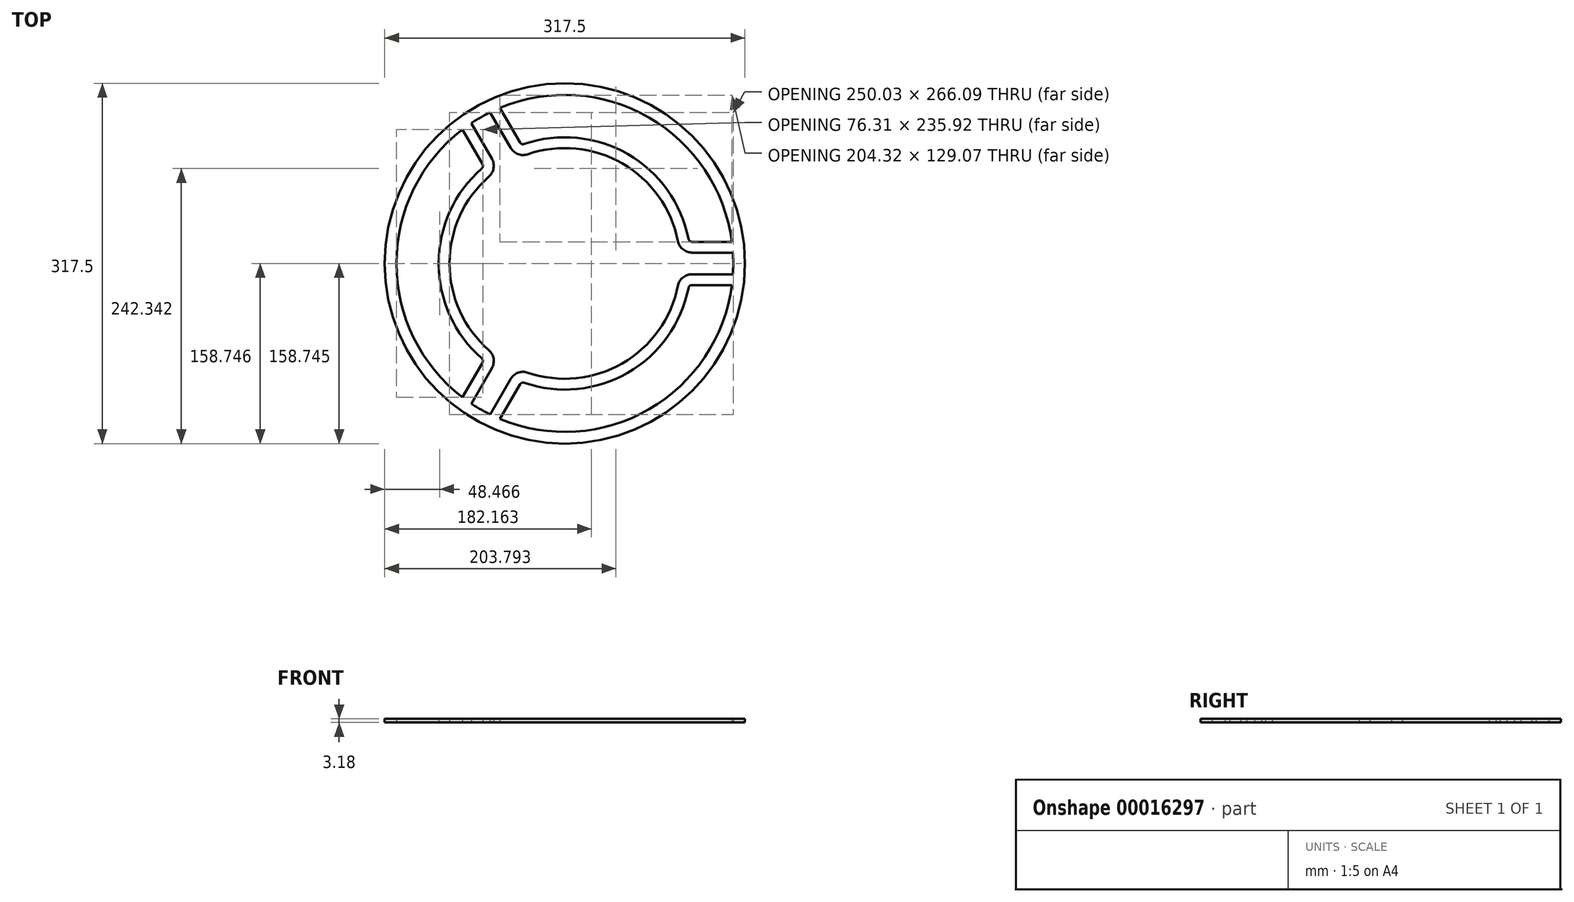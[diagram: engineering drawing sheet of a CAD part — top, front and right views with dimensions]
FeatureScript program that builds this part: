
annotation { "Feature Type Name" : "Feature", "Feature Type Description" : "" }
export const myFeature = defineFeature(function(context is Context, id is Id, definition is map)
    precondition{}
    {
        {
            var Q0;
            Q0=qCreatedBy(makeId("Top.planeOp"),FACE);
            var sketch = newSketch(context, id + "F0", { "sketchPlane" : qUnion([Q0])});
            skCircle(sketch, "E0", {"center": v(-34.22, 26.13) * mm, "radius": 158.75 * mm});
            skLineSegment(sketch, "E1", {"start": v(124.53, 26.13) * mm, "end": v(126.9, 26.13) * mm});
            skLineSegment(sketch, "E2.1.0", {"start": v(-113.6, 163.6) * mm, "end": v(-114.8, 165.67) * mm});
            skLineSegment(sketch, "E2.2.0", {"start": v(-113.6, -111.35) * mm, "end": v(-114.79, -113.42) * mm});
            skPoint(sketch, "E2.center", {"position": v(-34.23, 26.13) * mm});
            skArc(sketch, "E3", {"start": v(-101.17, 102.56) * mm, "mid": v(-135.82, 26.12) * mm, "end": v(-101.16, -50.3) * mm});
            skLineSegment(sketch, "E4.0", {"start": v(-82.04, 127.99) * mm, "end": v(-105.21, 168.12) * mm});
            skLineSegment(sketch, "E5.0", {"start": v(-98.54, 118.46) * mm, "end": v(-121.71, 158.6) * mm});
            skLineSegment(sketch, "E6.1.0", {"start": v(-98.53, -66.21) * mm, "end": v(-121.7, -106.35) * mm});
            skLineSegment(sketch, "E6.1.1", {"start": v(-82.03, -75.73) * mm, "end": v(-105.2, -115.87) * mm});
            skLineSegment(sketch, "E6.2.0", {"start": v(77.9, 16.61) * mm, "end": v(124.24, 16.61) * mm});
            skLineSegment(sketch, "E6.2.1", {"start": v(77.9, 35.66) * mm, "end": v(124.24, 35.66) * mm});
            skPoint(sketch, "E7.orphan", {"position": v(-34.22, 26.12) * mm});
            skArc(sketch, "E8.trimOffspring", {"start": v(65.44, 45.9) * mm, "mid": v(16.57, 114.12) * mm, "end": v(-66.95, 122.31) * mm});
            skArc(sketch, "E9.trimOffspring", {"start": v(-66.94, -70.06) * mm, "mid": v(16.58, -61.86) * mm, "end": v(65.44, 6.38) * mm});
            skPoint(sketch, "E10.visualSharp", {"position": v(-93.04, -56.71) * mm});
            skArc(sketch, "E10.filletArc", {"start": v(-98.53, -66.21) * mm, "mid": v(-97, -57.79) * mm, "end": v(-101.16, -50.3) * mm});
            skPoint(sketch, "E11.visualSharp", {"position": v(66.93, 16.61) * mm});
            skArc(sketch, "E11.filletArc", {"start": v(77.9, 16.61) * mm, "mid": v(69.84, 13.73) * mm, "end": v(65.44, 6.38) * mm});
            skPoint(sketch, "E12.visualSharp", {"position": v(66.93, 35.66) * mm});
            skArc(sketch, "E12.filletArc", {"start": v(65.44, 45.9) * mm, "mid": v(69.83, 38.55) * mm, "end": v(77.9, 35.66) * mm});
            skPoint(sketch, "E13.visualSharp", {"position": v(-76.56, 118.49) * mm});
            skArc(sketch, "E13.filletArc", {"start": v(-82.04, 127.99) * mm, "mid": v(-75.51, 122.45) * mm, "end": v(-66.95, 122.31) * mm});
            skPoint(sketch, "E14.visualSharp", {"position": v(-93.05, 108.96) * mm});
            skArc(sketch, "E14.filletArc", {"start": v(-101.17, 102.56) * mm, "mid": v(-97, 110.04) * mm, "end": v(-98.54, 118.46) * mm});
            skPoint(sketch, "E15.visualSharp", {"position": v(-76.54, -66.24) * mm});
            skArc(sketch, "E15.filletArc", {"start": v(-66.94, -70.06) * mm, "mid": v(-75.5, -70.2) * mm, "end": v(-82.03, -75.73) * mm});
            skLineSegment(sketch, "E16.0", {"start": v(-106.79, 113.7) * mm, "end": v(-124.33, 144.09) * mm});
            skArc(sketch, "E16.1", {"start": v(-107.44, 109.72) * mm, "mid": v(-106.4, 111.6) * mm, "end": v(-106.79, 113.7) * mm});
            skArc(sketch, "E16.2", {"start": v(-107.44, 109.72) * mm, "mid": v(-145.35, 26.12) * mm, "end": v(-107.43, -57.47) * mm});
            skArc(sketch, "E16.3", {"start": v(-106.78, -61.45) * mm, "mid": v(-106.4, -59.34) * mm, "end": v(-107.43, -57.47) * mm});
            skLineSegment(sketch, "E16.4", {"start": v(-106.78, -61.45) * mm, "end": v(-124.32, -91.83) * mm});
            skLineSegment(sketch, "E17.0", {"start": v(-73.8, 132.75) * mm, "end": v(-91.34, 163.14) * mm});
            skArc(sketch, "E17.1", {"start": v(-73.8, 132.75) * mm, "mid": v(-72.16, 131.36) * mm, "end": v(-70.02, 131.33) * mm});
            skArc(sketch, "E17.2", {"start": v(74.78, 47.74) * mm, "mid": v(21.33, 122.37) * mm, "end": v(-70.02, 131.33) * mm});
            skArc(sketch, "E17.3", {"start": v(74.78, 47.74) * mm, "mid": v(75.88, 45.9) * mm, "end": v(77.9, 45.19) * mm});
            skLineSegment(sketch, "E17.4", {"start": v(77.9, 45.19) * mm, "end": v(112.98, 45.19) * mm});
            skLineSegment(sketch, "E18.0", {"start": v(77.9, 7.09) * mm, "end": v(112.98, 7.09) * mm});
            skArc(sketch, "E18.1", {"start": v(77.9, 7.09) * mm, "mid": v(75.88, 6.36) * mm, "end": v(74.78, 4.53) * mm});
            skArc(sketch, "E18.2", {"start": v(-70, -79.08) * mm, "mid": v(21.34, -70.1) * mm, "end": v(74.78, 4.53) * mm});
            skArc(sketch, "E18.3", {"start": v(-70, -79.08) * mm, "mid": v(-72.15, -79.11) * mm, "end": v(-73.78, -80.5) * mm});
            skLineSegment(sketch, "E18.4", {"start": v(-73.78, -80.5) * mm, "end": v(-91.32, -110.88) * mm});
            skArc(sketch, "E19.0", {"start": v(-124.33, 144.09) * mm, "mid": v(-182.66, 26.12) * mm, "end": v(-124.32, -91.83) * mm});
            skArc(sketch, "E20.trimOffspring", {"start": v(-100.05, 159.17) * mm, "mid": v(-108.45, 154.67) * mm, "end": v(-116.54, 149.65) * mm});
            skArc(sketch, "E21.trimOffspring", {"start": v(113.9, 16.61) * mm, "mid": v(114.21, 26.14) * mm, "end": v(113.9, 35.66) * mm});
            skArc(sketch, "E22.trimOffspring", {"start": v(112.98, 45.19) * mm, "mid": v(39.99, 154.68) * mm, "end": v(-91.34, 163.14) * mm});
            skArc(sketch, "E23.trimOffspring", {"start": v(-116.53, -97.4) * mm, "mid": v(-108.43, -102.42) * mm, "end": v(-100.03, -106.92) * mm});
            skLineSegment(sketch, "E24.trimOffspring", {"start": v(-96.53, 172.14) * mm, "end": v(-98.15, 174.94) * mm});
            skLineSegment(sketch, "E25.trimOffspring", {"start": v(123.38, 45.19) * mm, "end": v(126.62, 45.19) * mm});
            skLineSegment(sketch, "E26.trimOffspring", {"start": v(-129.52, -100.84) * mm, "end": v(-131.14, -103.64) * mm});
            skLineSegment(sketch, "E27.trimOffspring", {"start": v(-129.53, 153.09) * mm, "end": v(-131.15, 155.9) * mm});
            skArc(sketch, "E28.1.0", {"start": v(-91.32, -110.88) * mm, "mid": v(40, -102.42) * mm, "end": v(112.98, 7.09) * mm});
            skLineSegment(sketch, "E28.anchor1", {"start": v(-34.22, 26.13) * mm, "end": v(-124.32, -91.83) * mm, "construction": true});
            skLineSegment(sketch, "E28.anchor2", {"start": v(-34.22, 26.13) * mm, "end": v(112.98, 7.09) * mm, "construction": true});
            skLineSegment(sketch, "E29.trimOffspring", {"start": v(123.38, 7.09) * mm, "end": v(126.62, 7.09) * mm});
            skLineSegment(sketch, "E30.trimOffspring", {"start": v(-96.52, -119.89) * mm, "end": v(-98.14, -122.7) * mm});
            skSolve(sketch);
        }
        {
            var Q0;
            Q0=makeQuery(id+"F0.imprint","IMPRINT",FACE,{"disambiguationData":[TD([[makeQuery(id+"F0.imprint","IMPRINT",EDGE,{"derivedFrom":sQuery(id+"F0.wireOp",EDGE,"E3")}),-1.0]])]});
            var Q1;
            {var subQ0=sQuery(id+"F0.wireOp",EDGE,"E20.trimOffspring");Q1=makeQuery(id+"F0.imprint","IMPRINT",FACE,{"disambiguationData":[TD([[makeQuery(id+"F0.imprint","IMPRINT",EDGE,{"derivedFrom":subQ0}),-1.0]])]});}
            var Q2;
            Q2=makeQuery(id+"F0.imprint","IMPRINT",FACE,{"disambiguationData":[TD([[makeQuery(id+"F0.imprint","IMPRINT",EDGE,{"derivedFrom":sQuery(id+"F0.wireOp",EDGE,"E8.trimOffspring")}),-1.0]])]});
            var Q3;
            {var subQ0=sQuery(id+"F0.wireOp",EDGE,"E21.trimOffspring");Q3=makeQuery(id+"F0.imprint","IMPRINT",FACE,{"disambiguationData":[TD([[makeQuery(id+"F0.imprint","IMPRINT",EDGE,{"derivedFrom":subQ0}),-1.0]])]});}
            var Q4;
            Q4=makeQuery(id+"F0.imprint","IMPRINT",FACE,{"disambiguationData":[TD([[makeQuery(id+"F0.imprint","IMPRINT",EDGE,{"derivedFrom":sQuery(id+"F0.wireOp",EDGE,"E9.trimOffspring")}),-1.0]])]});
            var Q5;
            {var subQ0=sQuery(id+"F0.wireOp",EDGE,"E23.trimOffspring");Q5=makeQuery(id+"F0.imprint","IMPRINT",FACE,{"disambiguationData":[TD([[makeQuery(id+"F0.imprint","IMPRINT",EDGE,{"derivedFrom":subQ0}),-1.0]])]});}
            extrude(context, id + "F1", {"entities" : qUnion([Q0, Q1, Q2, Q3, Q4, Q5]), "depth" : 3.17 * mm});
        }
    });
